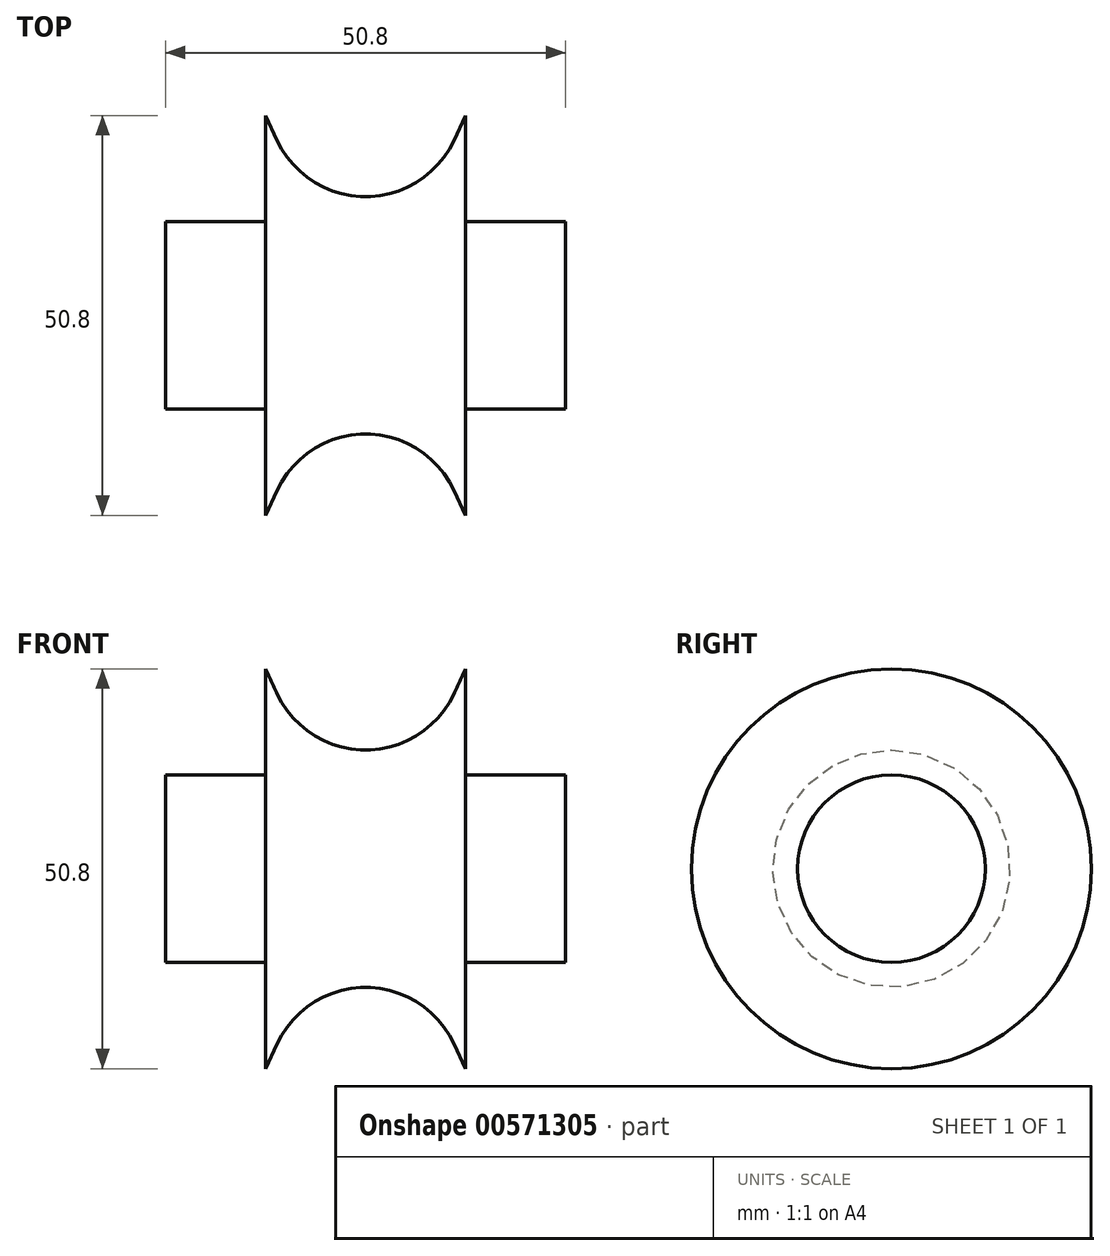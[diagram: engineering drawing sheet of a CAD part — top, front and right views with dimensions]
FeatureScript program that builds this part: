
annotation { "Feature Type Name" : "Feature", "Feature Type Description" : "" }
export const myFeature = defineFeature(function(context is Context, id is Id, definition is map)
    precondition{}
    {
        {
            var Q0;
            Q0=qCreatedBy(makeId("Front.planeOp"),FACE);
            var sketch = newSketch(context, id + "F0", { "sketchPlane" : qUnion([Q0])});
            skLineSegment(sketch, "E0", {"start": v(0, 0) * mm, "end": v(25.4, 0) * mm});
            skLineSegment(sketch, "E1", {"start": v(25.4, 0) * mm, "end": v(25.4, 11.91) * mm});
            skLineSegment(sketch, "E2", {"start": v(25.4, 11.91) * mm, "end": v(12.7, 11.91) * mm});
            skLineSegment(sketch, "E3", {"start": v(12.7, 11.91) * mm, "end": v(12.7, 25.4) * mm});
            skLineSegment(sketch, "E4", {"start": v(12.7, 25.4) * mm, "end": v(11.22, 22.22) * mm});
            skLineSegment(sketch, "E5.MirrorCS", {"start": v(-12.7, 11.91) * mm, "end": v(-12.7, 25.4) * mm});
            skLineSegment(sketch, "E6.MirrorCS", {"start": v(-12.7, 25.4) * mm, "end": v(-11.22, 22.22) * mm});
            skLineSegment(sketch, "E7.MirrorCS", {"start": v(-25.4, 11.91) * mm, "end": v(-12.7, 11.91) * mm});
            skLineSegment(sketch, "E8.MirrorCS", {"start": v(-25.4, 0) * mm, "end": v(-25.4, 11.91) * mm});
            skLineSegment(sketch, "E9.MirrorCS", {"start": v(0, 0) * mm, "end": v(-25.4, 0) * mm});
            skArc(sketch, "E10", {"start": v(-11.22, 22.22) * mm, "mid": v(0, 15.08) * mm, "end": v(11.22, 22.23) * mm});
            skLineSegment(sketch, "E11", {"start": v(-34.58, 0) * mm, "end": v(37.14, 0) * mm, "construction": true});
            skSolve(sketch);
        }
        {
            var Q0;
            Q0 = qSketchRegion(id + "F0", true);
            var Q1;
            Q1=sQuery(id+"F0.wireOp",EDGE,"E11");
            revolve(context, id + "F1", {"entities" : qUnion([Q0]), "axis" : qUnion([Q1]), "revolveType" : RevolveType.FULL});
        }
    });
